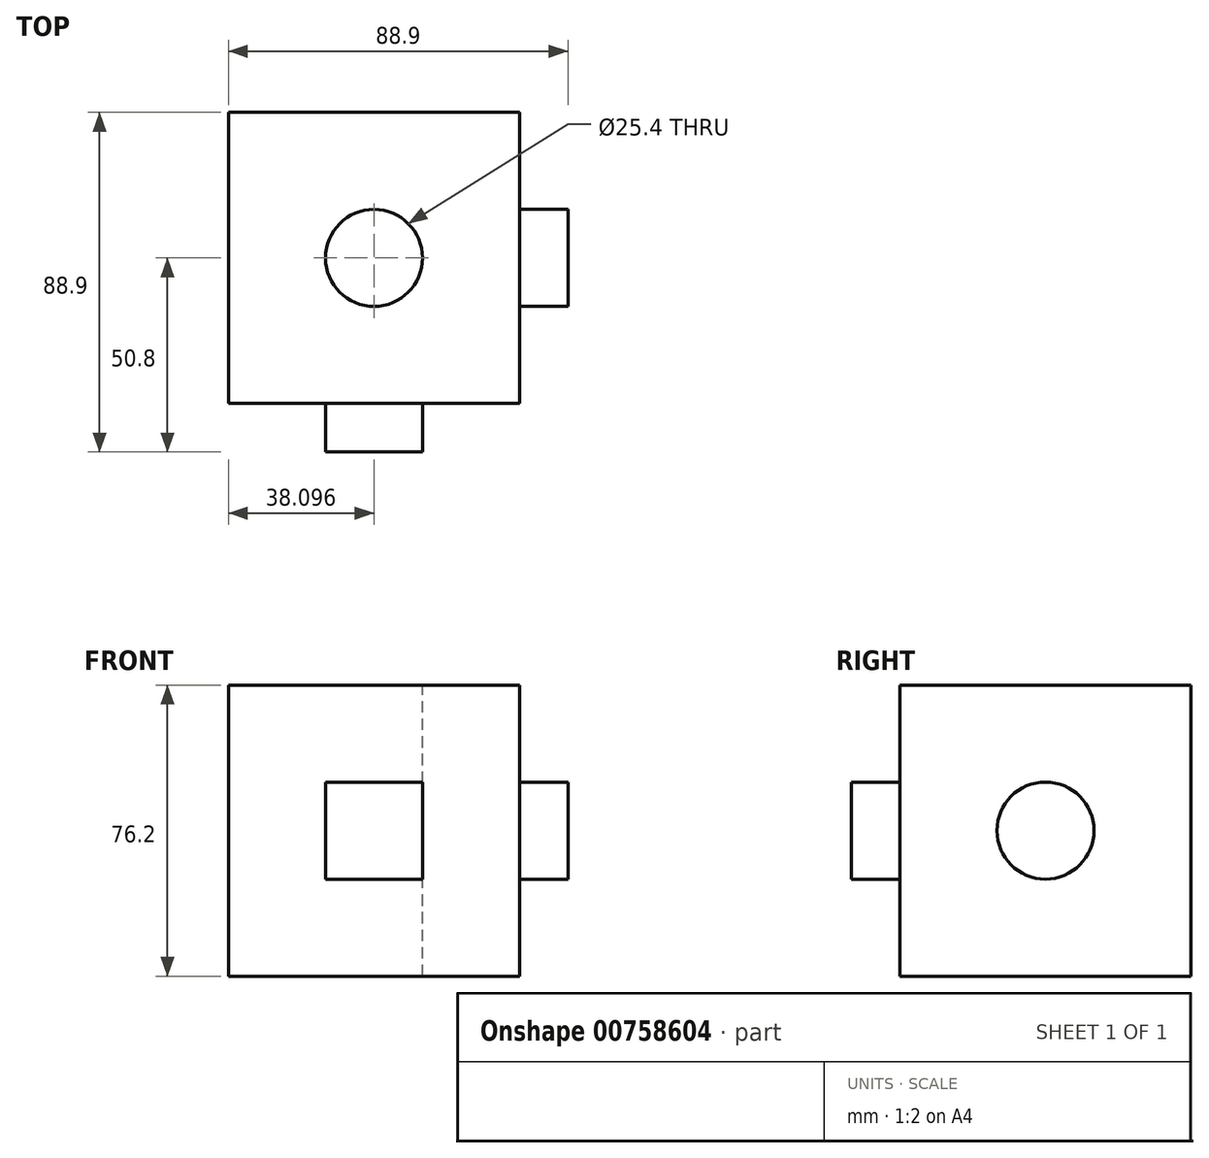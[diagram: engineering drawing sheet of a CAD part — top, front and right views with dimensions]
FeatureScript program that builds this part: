
annotation { "Feature Type Name" : "Feature", "Feature Type Description" : "" }
export const myFeature = defineFeature(function(context is Context, id is Id, definition is map)
    precondition{}
    {
        {
            var Q0;
            Q0=qCreatedBy(makeId("Front.planeOp"),FACE);
            var sketch = newSketch(context, id + "F0", { "sketchPlane" : qUnion([Q0])});
            skLineSegment(sketch, "E0.bottom", {"start": v(-36.1, 50.01) * mm, "end": v(40.1, 50.01) * mm});
            skLineSegment(sketch, "E0.top", {"start": v(-36.1, -26.19) * mm, "end": v(40.1, -26.19) * mm});
            skLineSegment(sketch, "E0.left", {"start": v(-36.1, 50.01) * mm, "end": v(-36.1, -26.19) * mm});
            skLineSegment(sketch, "E0.right", {"start": v(40.1, 50.01) * mm, "end": v(40.1, -26.19) * mm});
            skSolve(sketch);
        }
        {
            var Q0;
            Q0=makeQuery(id+"F0.imprint","IMPRINT",FACE,{"disambiguationData":[TD([[makeQuery(id+"F0.imprint","IMPRINT",EDGE,{"derivedFrom":sQuery(id+"F0.wireOp",EDGE,"E0.bottom")}),-1.0]])]});
            extrude(context, id + "F1", {"entities" : qUnion([Q0]), "depth" : 76.2 * mm, "offsetDistance" : 25.4 * mm});
        }
        {
            var Q0;
            Q0=makeQuery(id+"F1.opExtrude","CAP_FACE",FACE,{"disambiguationData":[OSD([sQuery(id+"F0.wireOp",EDGE,"E0.bottom"),sQuery(id+"F0.wireOp",EDGE,"E0.top"),sQuery(id+"F0.wireOp",EDGE,"E0.left"),sQuery(id+"F0.wireOp",EDGE,"E0.right")])],"isStart":false});
            var sketch = newSketch(context, id + "F2", { "sketchPlane" : qUnion([Q0])});
            skLineSegment(sketch, "E1.bottom", {"start": v(-10.7, 24.61) * mm, "end": v(14.7, 24.61) * mm});
            skLineSegment(sketch, "E1.top", {"start": v(-10.7, -0.79) * mm, "end": v(14.7, -0.79) * mm});
            skLineSegment(sketch, "E1.left", {"start": v(-10.7, 24.61) * mm, "end": v(-10.7, -0.79) * mm});
            skLineSegment(sketch, "E1.right", {"start": v(14.7, 24.61) * mm, "end": v(14.7, -0.79) * mm});
            skSolve(sketch);
        }
        {
            var Q0;
            Q0=makeQuery(id+"F2.imprint","IMPRINT",FACE,{"disambiguationData":[TD([[makeQuery(id+"F2.imprint","IMPRINT",EDGE,{"derivedFrom":sQuery(id+"F2.wireOp",EDGE,"E1.bottom")}),-1.0]])]});
            extrude(context, id + "F3", {"entities" : qUnion([Q0]), "operationType" : NewBodyOperationType.ADD, "depth" : 12.7 * mm, "offsetDistance" : 25.4 * mm});
        }
        {
            var Q0;
            Q0=makeQuery(id+"F1.opExtrude","SWEPT_FACE",FACE,{"disambiguationData":[OSD([sQuery(id+"F0.wireOp",EDGE,"E0.right")])]});
            var sketch = newSketch(context, id + "F4", { "sketchPlane" : qUnion([Q0])});
            skCircle(sketch, "E2", {"center": v(-38.1, 11.91) * mm, "radius": 12.7 * mm});
            skSolve(sketch);
        }
        {
            var Q0;
            Q0=makeQuery(id+"F4.imprint","IMPRINT",FACE,{"disambiguationData":[TD([[makeQuery(id+"F4.imprint","IMPRINT",EDGE,{"derivedFrom":sQuery(id+"F4.wireOp",EDGE,"E2")}),1.0]])]});
            extrude(context, id + "F5", {"entities" : qUnion([Q0]), "operationType" : NewBodyOperationType.ADD, "depth" : 12.7 * mm, "offsetDistance" : 25.4 * mm});
        }
        {
            var Q0;
            Q0=makeQuery(id+"F1.opExtrude","SWEPT_FACE",FACE,{"disambiguationData":[OSD([sQuery(id+"F0.wireOp",EDGE,"E0.bottom")])]});
            var sketch = newSketch(context, id + "F6", { "sketchPlane" : qUnion([Q0])});
            skPoint(sketch, "E3", {"position": v(2, -38.1) * mm});
            skSolve(sketch);
        }
        {
            var Q0;
            Q0=sQuery(id+"F6.wireOp",VERTEX,"E3");
            var Q1;
            Q1=makeQuery(id+"F1.opExtrude","SWEPT_BODY",BODY,{"disambiguationData":[OSD([sQuery(id+"F0.wireOp",EDGE,"E0.bottom"),sQuery(id+"F0.wireOp",EDGE,"E0.top"),sQuery(id+"F0.wireOp",EDGE,"E0.left"),sQuery(id+"F0.wireOp",EDGE,"E0.right")])]});
            hole(context, id + "F7", {"style" : HoleStyle.SIMPLE, "endStyle" : HoleEndStyle.THROUGH, "holeDiameter" : 25.4 * mm, "majorDiameter" : 6.35 * mm, "isTappedThrough" : true, "tappedDepth" : 12.7 * mm, "tapClearance" : 3, "locations" : qUnion([Q0]), "scope" : qUnion([Q1])});
        }
    });
